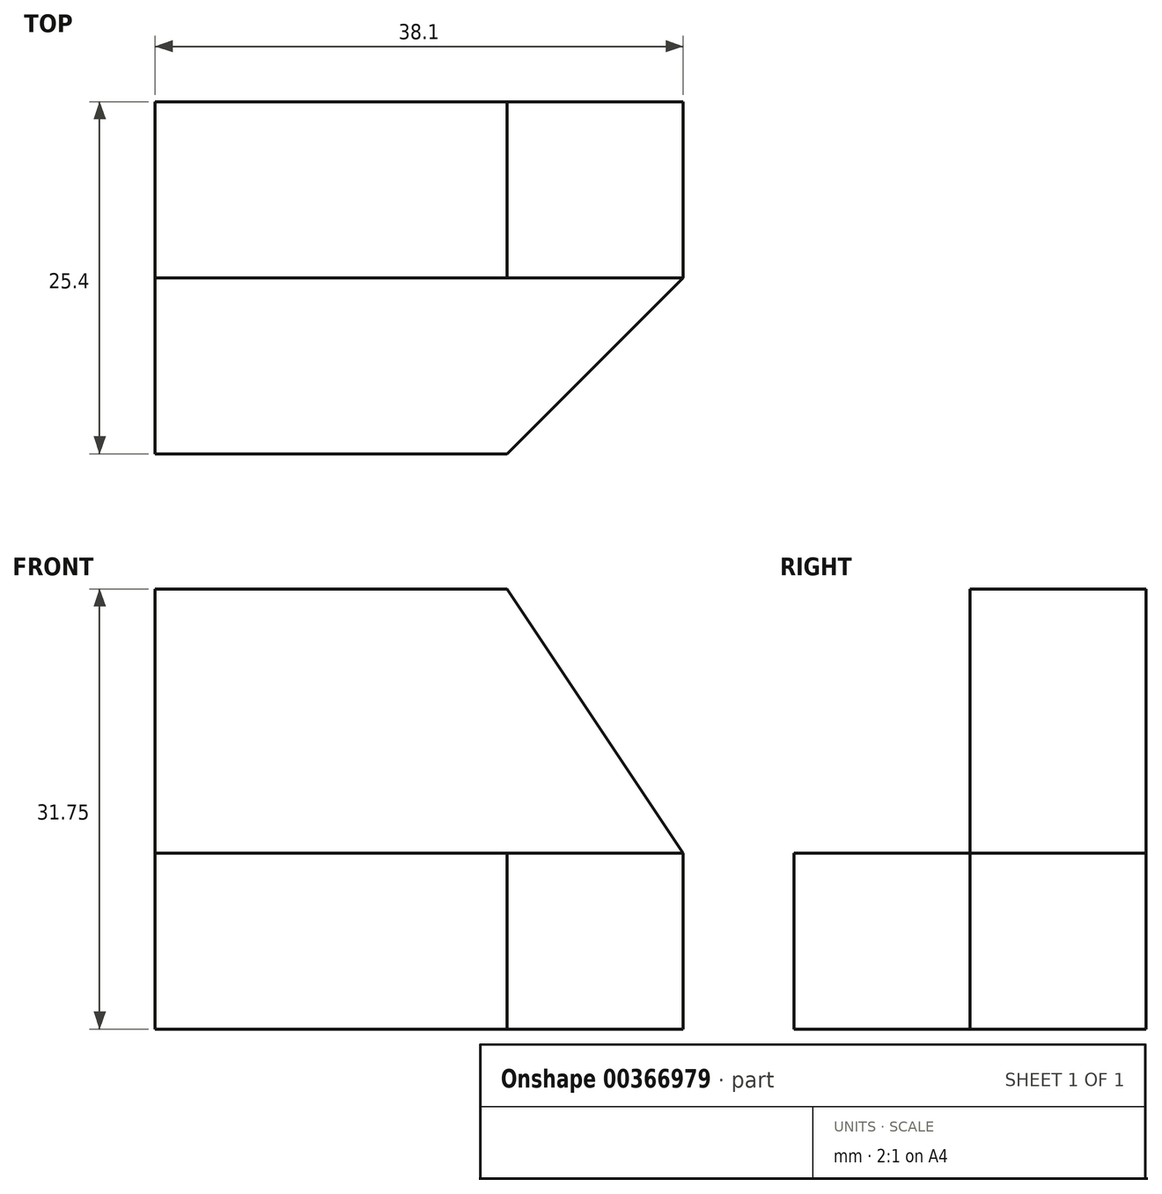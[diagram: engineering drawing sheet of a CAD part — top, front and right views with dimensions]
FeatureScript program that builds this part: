
annotation { "Feature Type Name" : "Feature", "Feature Type Description" : "" }
export const myFeature = defineFeature(function(context is Context, id is Id, definition is map)
    precondition{}
    {
        {
            var Q0;
            Q0=qCreatedBy(makeId("Right.planeOp"),FACE);
            var sketch = newSketch(context, id + "F0", { "sketchPlane" : qUnion([Q0])});
            skLineSegment(sketch, "E0", {"start": v(0, 0) * mm, "end": v(25.4, 0) * mm});
            skLineSegment(sketch, "E1", {"start": v(25.4, 0) * mm, "end": v(25.4, 31.75) * mm});
            skLineSegment(sketch, "E2", {"start": v(25.4, 31.75) * mm, "end": v(12.7, 31.75) * mm});
            skLineSegment(sketch, "E3", {"start": v(12.7, 31.75) * mm, "end": v(12.7, 12.7) * mm});
            skLineSegment(sketch, "E4", {"start": v(12.7, 12.7) * mm, "end": v(0, 12.7) * mm});
            skLineSegment(sketch, "E5", {"start": v(0, 12.7) * mm, "end": v(0, 0) * mm});
            skSolve(sketch);
        }
        {
            var Q0;
            Q0 = qSketchRegion(id + "F0", true);
            extrude(context, id + "F1", {"entities" : qUnion([Q0]), "depth" : 38.1 * mm});
        }
        {
            var Q0;
            Q0=makeQuery(id+"F1.opExtrude","SWEPT_FACE",FACE,{"disambiguationData":[OSD([sQuery(id+"F0.wireOp",EDGE,"E3")])]});
            var sketch = newSketch(context, id + "F2", { "sketchPlane" : qUnion([Q0])});
            skLineSegment(sketch, "E6", {"start": v(25.4, 31.75) * mm, "end": v(38.1, 12.7) * mm});
            skSolve(sketch);
        }
        {
            var Q0;
            {var subQ0=sQuery(id+"F2.wireOp",EDGE,"E6");Q0=makeQuery(id+"F2.imprint","IMPRINT",FACE,{"disambiguationData":[TD([[makeQuery(id+"F2.imprint","IMPRINT",EDGE,{"derivedFrom":subQ0}),1.0]])]});}
            extrude(context, id + "F3", {"entities" : qUnion([Q0]), "operationType" : NewBodyOperationType.REMOVE, "oppositeDirection" : true, "depth" : 12.7 * mm});
        }
        {
            var Q0;
            Q0=makeQuery(id+"F1.opExtrude","SWEPT_FACE",FACE,{"disambiguationData":[OSD([sQuery(id+"F0.wireOp",EDGE,"E4")])]});
            var sketch = newSketch(context, id + "F4", { "sketchPlane" : qUnion([Q0])});
            skLineSegment(sketch, "E7", {"start": v(38.1, 12.7) * mm, "end": v(25.4, 0) * mm});
            skSolve(sketch);
        }
        {
            var Q0;
            {var subQ0=sQuery(id+"F4.wireOp",EDGE,"E7");Q0=makeQuery(id+"F4.imprint","IMPRINT",FACE,{"disambiguationData":[TD([[makeQuery(id+"F4.imprint","IMPRINT",EDGE,{"derivedFrom":subQ0}),1.0]])]});}
            extrude(context, id + "F5", {"entities" : qUnion([Q0]), "operationType" : NewBodyOperationType.REMOVE, "oppositeDirection" : true, "depth" : 12.7 * mm});
        }
    });
